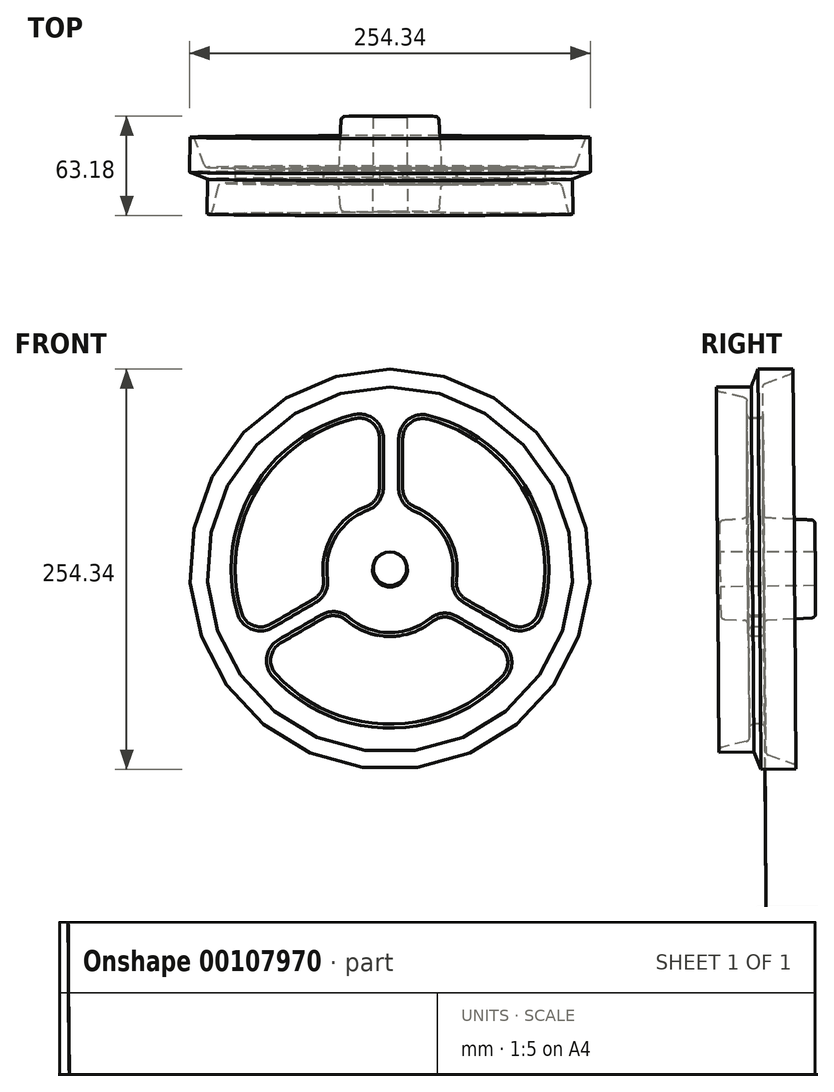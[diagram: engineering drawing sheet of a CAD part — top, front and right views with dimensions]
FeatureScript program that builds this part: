
annotation { "Feature Type Name" : "Feature", "Feature Type Description" : "" }
export const myFeature = defineFeature(function(context is Context, id is Id, definition is map)
    precondition{}
    {
        {
            var Q0;
            Q0=qCreatedBy(makeId("Right.planeOp"),FACE);
            var sketch = newSketch(context, id + "F0", { "sketchPlane" : qUnion([Q0])});
            skLineSegment(sketch, "E0", {"start": v(162.7, 1.24) * mm, "end": v(-180.07, -1.38) * mm, "construction": true});
            skLineSegment(sketch, "E1", {"start": v(-17.14, 10.98) * mm, "end": v(43.18, 10.98) * mm});
            skLineSegment(sketch, "E2", {"start": v(43.18, 10.98) * mm, "end": v(43.18, 28.87) * mm});
            skLineSegment(sketch, "E3", {"start": v(10.16, 35.14) * mm, "end": v(10.16, 115.78) * mm});
            skLineSegment(sketch, "E4", {"start": v(40.75, 31.4) * mm, "end": v(12.6, 32.6) * mm});
            skLineSegment(sketch, "E5", {"start": v(6.97, 127.23) * mm, "end": v(2.67, 115.95) * mm});
            skLineSegment(sketch, "E6", {"start": v(0, 34.83) * mm, "end": v(0, 106.8) * mm});
            skLineSegment(sketch, "E7", {"start": v(-17.14, 10.98) * mm, "end": v(-17.14, 28.93) * mm});
            skLineSegment(sketch, "E8", {"start": v(-14.77, 31.46) * mm, "end": v(-2.37, 32.3) * mm});
            skLineSegment(sketch, "E9", {"start": v(6.97, 127.23) * mm, "end": v(29.2, 127.23) * mm});
            skLineSegment(sketch, "E10", {"start": v(29.2, 127.23) * mm, "end": v(29.2, 126.36) * mm});
            skLineSegment(sketch, "E11", {"start": v(27.54, 123.98) * mm, "end": v(11.82, 118.16) * mm});
            skLineSegment(sketch, "E12", {"start": v(2.67, 115.95) * mm, "end": v(-19.56, 115.95) * mm});
            skLineSegment(sketch, "E13", {"start": v(-19.56, 115.95) * mm, "end": v(-19.56, 115.26) * mm});
            skLineSegment(sketch, "E14", {"start": v(-17.58, 112.78) * mm, "end": v(-1.98, 109.27) * mm});
            skArc(sketch, "E15.filletArc", {"start": v(10.16, 35.14) * mm, "mid": v(10.87, 33.38) * mm, "end": v(12.6, 32.6) * mm});
            skArc(sketch, "E16.filletArc", {"start": v(-2.37, 32.3) * mm, "mid": v(-0.68, 33.1) * mm, "end": v(0, 34.83) * mm});
            skPoint(sketch, "E17.visualSharp", {"position": v(-17.14, 31.3) * mm});
            skArc(sketch, "E17.filletArc", {"start": v(-14.77, 31.46) * mm, "mid": v(-16.46, 30.66) * mm, "end": v(-17.14, 28.93) * mm});
            skPoint(sketch, "E18.visualSharp", {"position": v(43.18, 31.3) * mm});
            skArc(sketch, "E18.filletArc", {"start": v(43.18, 28.87) * mm, "mid": v(42.48, 30.63) * mm, "end": v(40.75, 31.4) * mm});
            skArc(sketch, "E19.filletArc", {"start": v(11.82, 118.16) * mm, "mid": v(10.62, 117.23) * mm, "end": v(10.16, 115.78) * mm});
            skArc(sketch, "E20.filletArc", {"start": v(0, 106.8) * mm, "mid": v(-0.55, 108.38) * mm, "end": v(-1.98, 109.27) * mm});
            skArc(sketch, "E21.filletArc", {"start": v(27.54, 123.98) * mm, "mid": v(28.74, 124.9) * mm, "end": v(29.2, 126.36) * mm});
            skArc(sketch, "E22.filletArc", {"start": v(-19.56, 115.26) * mm, "mid": v(-19, 113.67) * mm, "end": v(-17.58, 112.78) * mm});
            skSolve(sketch);
        }
        {
            var Q0;
            Q0=makeQuery(id+"F0.imprint","IMPRINT",FACE,{"disambiguationData":[TD([[makeQuery(id+"F0.imprint","IMPRINT",EDGE,{"derivedFrom":sQuery(id+"F0.wireOp",EDGE,"E1")}),1.0]])]});
            var Q1;
            Q1=sQuery(id+"F0.wireOp",EDGE,"E0");
            revolve(context, id + "F1", {"entities" : qUnion([Q0]), "axis" : qUnion([Q1]), "revolveType" : RevolveType.FULL});
        }
        {
            var Q0;
            Q0=qCreatedBy(makeId("Front.planeOp"),FACE);
            var sketch = newSketch(context, id + "F2", { "sketchPlane" : qUnion([Q0])});
            skArc(sketch, "E23", {"start": v(-72.48, -66.45) * mm, "mid": v(-0.85, -98.33) * mm, "end": v(71.33, -67.69) * mm});
            skArc(sketch, "E24", {"start": v(-27.72, -32.42) * mm, "mid": v(-0.57, -42.65) * mm, "end": v(26.85, -33.15) * mm});
            skLineSegment(sketch, "E25", {"start": v(-6.77, 83.4) * mm, "end": v(-6.77, 51.82) * mm});
            skLineSegment(sketch, "E26", {"start": v(8.07, 83.08) * mm, "end": v(8.07, 51.31) * mm});
            skLineSegment(sketch, "E27", {"start": v(0, 0) * mm, "end": v(-134.6, -77.71) * mm, "construction": true});
            skLineSegment(sketch, "E28", {"start": v(0, 0) * mm, "end": v(0, 147.26) * mm, "construction": true});
            skLineSegment(sketch, "E29", {"start": v(0, 0) * mm, "end": v(180, -103.92) * mm, "construction": true});
            skLineSegment(sketch, "E30", {"start": v(-48.4, -18.85) * mm, "end": v(-75.86, -34.82) * mm});
            skLineSegment(sketch, "E31", {"start": v(-42.36, -31.1) * mm, "end": v(-69.5, -46.89) * mm});
            skLineSegment(sketch, "E32", {"start": v(48.46, -19.15) * mm, "end": v(75.96, -34.84) * mm});
            skLineSegment(sketch, "E33", {"start": v(41.25, -32.05) * mm, "end": v(68.52, -47.98) * mm});
            skArc(sketch, "E34.trimOffspring", {"start": v(42.2, -6.26) * mm, "mid": v(37.03, 21.18) * mm, "end": v(16, 39.54) * mm});
            skArc(sketch, "E35.trimOffspring", {"start": v(94.45, -27.34) * mm, "mid": v(85.24, 49.03) * mm, "end": v(23.85, 95.4) * mm});
            skArc(sketch, "E36.trimOffspring", {"start": v(-22.35, 95.76) * mm, "mid": v(-84.86, 49.68) * mm, "end": v(-94.44, -27.38) * mm});
            skArc(sketch, "E37.trimOffspring", {"start": v(-15, 39.93) * mm, "mid": v(-36.71, 21.73) * mm, "end": v(-42.22, -6.07) * mm});
            skPoint(sketch, "E38.visualSharp", {"position": v(-6.77, 42.12) * mm});
            skArc(sketch, "E38.filletArc", {"start": v(-15, 39.93) * mm, "mid": v(-9.03, 44.6) * mm, "end": v(-6.77, 51.82) * mm});
            skPoint(sketch, "E39.visualSharp", {"position": v(-6.77, 98.1) * mm});
            skArc(sketch, "E39.filletArc", {"start": v(-6.77, 83.4) * mm, "mid": v(-11.57, 93.34) * mm, "end": v(-22.35, 95.76) * mm});
            skPoint(sketch, "E40.visualSharp", {"position": v(8.07, 98) * mm});
            skArc(sketch, "E40.filletArc", {"start": v(23.85, 95.4) * mm, "mid": v(12.95, 93.09) * mm, "end": v(8.07, 83.08) * mm});
            skPoint(sketch, "E41.visualSharp", {"position": v(8.07, 41.89) * mm});
            skArc(sketch, "E41.filletArc", {"start": v(8.07, 51.31) * mm, "mid": v(10.24, 44.22) * mm, "end": v(16, 39.54) * mm});
            skPoint(sketch, "E42.visualSharp", {"position": v(40.15, -14.4) * mm});
            skArc(sketch, "E42.filletArc", {"start": v(42.2, -6.26) * mm, "mid": v(43.34, -13.67) * mm, "end": v(48.46, -19.15) * mm});
            skPoint(sketch, "E43.visualSharp", {"position": v(88.82, -42.18) * mm});
            skArc(sketch, "E43.filletArc", {"start": v(75.96, -34.84) * mm, "mid": v(87.03, -35.58) * mm, "end": v(94.45, -27.34) * mm});
            skPoint(sketch, "E44.visualSharp", {"position": v(-88.76, -42.32) * mm});
            skArc(sketch, "E44.filletArc", {"start": v(-94.44, -27.38) * mm, "mid": v(-86.97, -35.63) * mm, "end": v(-75.86, -34.82) * mm});
            skPoint(sketch, "E45.visualSharp", {"position": v(-40.26, -14.1) * mm});
            skArc(sketch, "E45.filletArc", {"start": v(-48.4, -18.85) * mm, "mid": v(-43.36, -13.4) * mm, "end": v(-42.22, -6.07) * mm});
            skPoint(sketch, "E46.visualSharp", {"position": v(-33.75, -26.09) * mm});
            skArc(sketch, "E46.filletArc", {"start": v(-27.72, -32.42) * mm, "mid": v(-34.83, -29.42) * mm, "end": v(-42.36, -31.1) * mm});
            skPoint(sketch, "E47.visualSharp", {"position": v(32.9, -27.16) * mm});
            skArc(sketch, "E47.filletArc", {"start": v(41.25, -32.05) * mm, "mid": v(33.88, -30.35) * mm, "end": v(26.85, -33.15) * mm});
            skPoint(sketch, "E48.visualSharp", {"position": v(81.24, -55.4) * mm});
            skArc(sketch, "E48.filletArc", {"start": v(71.33, -67.69) * mm, "mid": v(74.69, -57.16) * mm, "end": v(68.52, -47.98) * mm});
            skPoint(sketch, "E49.visualSharp", {"position": v(-82.05, -54.19) * mm});
            skArc(sketch, "E49.filletArc", {"start": v(-69.5, -46.89) * mm, "mid": v(-75.68, -55.96) * mm, "end": v(-72.48, -66.45) * mm});
            skSolve(sketch);
        }
        {
            var Q0;
            Q0=makeQuery(id+"F2.imprint","IMPRINT",FACE,{"disambiguationData":[TD([[makeQuery(id+"F2.imprint","IMPRINT",EDGE,{"derivedFrom":sQuery(id+"F2.wireOp",EDGE,"E25")}),-1.0]])]});
            var Q1;
            Q1=makeQuery(id+"F2.imprint","IMPRINT",FACE,{"disambiguationData":[TD([[makeQuery(id+"F2.imprint","IMPRINT",EDGE,{"derivedFrom":sQuery(id+"F2.wireOp",EDGE,"E26")}),1.0]])]});
            var Q2;
            Q2=makeQuery(id+"F2.imprint","IMPRINT",FACE,{"disambiguationData":[TD([[makeQuery(id+"F2.imprint","IMPRINT",EDGE,{"derivedFrom":sQuery(id+"F2.wireOp",EDGE,"E23")}),1.0]])]});
            extrude(context, id + "F3", {"entities" : qUnion([Q0, Q1, Q2]), "operationType" : NewBodyOperationType.REMOVE, "endBound" : BoundingType.THROUGH_ALL, "oppositeDirection" : true, "depth" : 25.4 * mm});
        }
        {
            var Q0;
            Q0=makeQuery(id+"F1.opRevolve","SWEPT_FACE",FACE,{"disambiguationData":[OSD([sQuery(id+"F0.wireOp",EDGE,"E6")])]});
            var Q1;
            Q1=makeQuery(id+"F1.opRevolve","SWEPT_FACE",FACE,{"disambiguationData":[OSD([sQuery(id+"F0.wireOp",EDGE,"E3")])]});
            fillet(context, id + "F4", {"entities" : qUnion([Q0, Q1]), "radius" : 2.54 * mm, "tangentPropagation" : true, "allowEdgeOverflow" : false});
        }
    });
